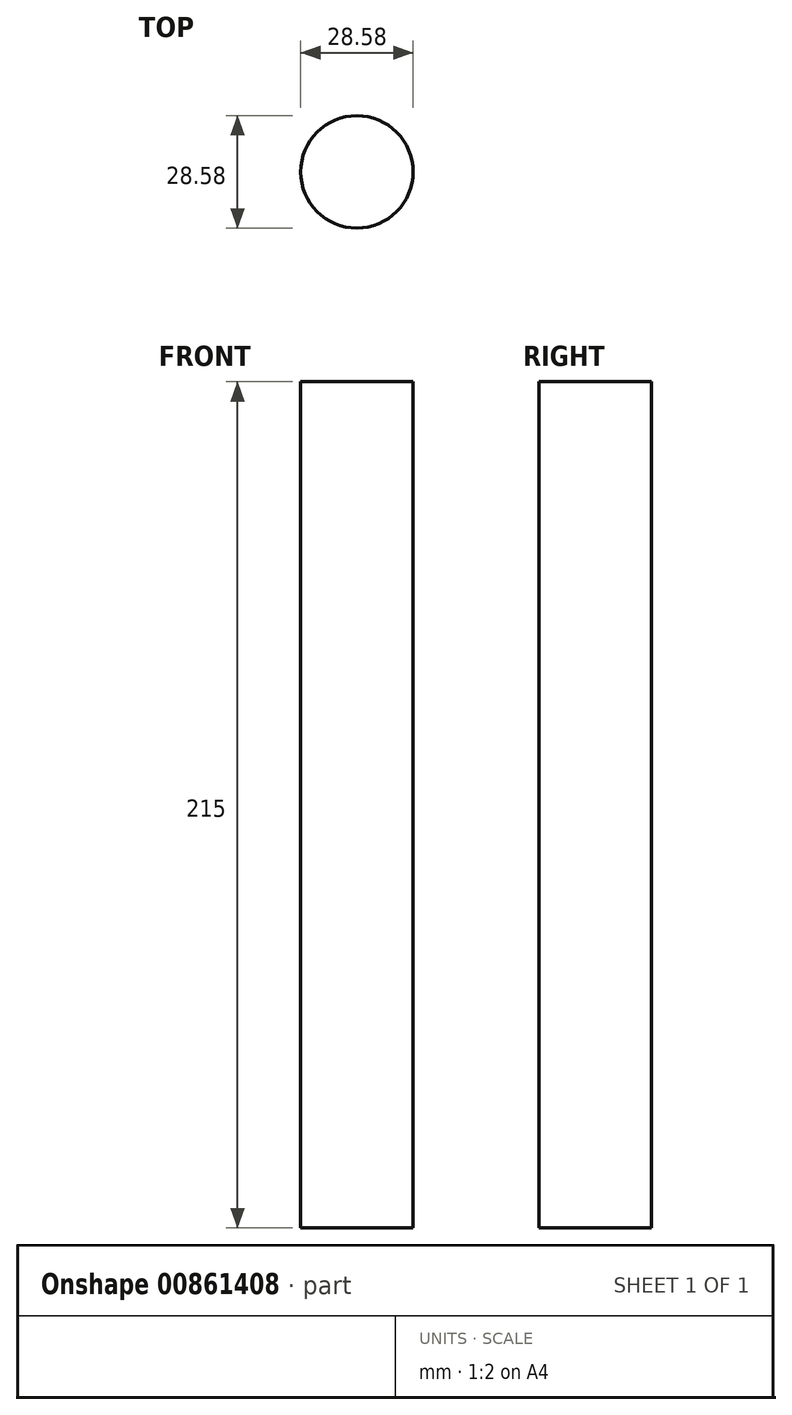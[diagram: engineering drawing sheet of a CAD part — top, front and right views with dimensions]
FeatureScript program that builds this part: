
annotation { "Feature Type Name" : "Feature", "Feature Type Description" : "" }
export const myFeature = defineFeature(function(context is Context, id is Id, definition is map)
    precondition{}
    {
        {
            var Q0;
            Q0=qCreatedBy(makeId("Top.planeOp"),FACE);
            var sketch = newSketch(context, id + "F0", { "sketchPlane" : qUnion([Q0])});
            skCircle(sketch, "E0", {"center": v(0, 0) * mm, "radius": 14.29 * mm});
            skSolve(sketch);
        }
        {
            var Q0;
            Q0 = qSketchRegion(id + "F0", true);
            extrude(context, id + "F1", {"entities" : qUnion([Q0]), "depth" : 215 * mm, "offsetDistance" : 25 * mm});
        }
    });
